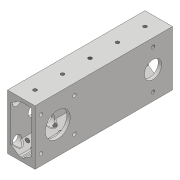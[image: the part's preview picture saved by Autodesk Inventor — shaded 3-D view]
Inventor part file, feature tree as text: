
AUTODESK INVENTOR PART (.ipt)
format: ipt  version: 2018 (Build 220112000, 112)  size: 839,680 bytes
history: native  units: mm
features: sketch x7, hole x5, extrude x3, chamfer x3, other x3, fillet x2, shell x1, pattern_linear x1, mirror x1, reference x1, projected_geometry x1
ambient origin geometry x8: Origin, YZ Plane, XZ Plane, XY Plane, X Axis, Y Axis, Z Axis, Center Point
bodies: Solid1 (feature_tree)
feature tree (28):
  extrude  "Extrusion1"  Depth=25.4mm
  shell  "Shell1"  Thickness=127.0mm
  chamfer  "Chamfer1"  Distance=23.0mm
  chamfer  "Chamfer2"  Distance=50.8mm
  chamfer  "Chamfer3"  Distance=16.0mm
  sketch  "Sketch2"  dims[d4=3.175mm]
  hole  "Hole1"  [1 undecoded]
  hole  "Hole2"  [1 undecoded]
  extrude  "Extrusion2"  Depth=3.0mm
  extrude  "Extrusion3"  Depth=3.0mm
  hole  "Hole4"  [1 undecoded]
  hole  "Hole5"  [1 undecoded]
  fillet  "Fillet3"  Radius=8.0mm
  pattern_linear  "Rectangular Pattern1"  Spacing1=1.5mm  [1 undecoded]
  mirror  "Mirror1"
  hole  "Hole6"  [1 undecoded]
  fillet  "Fillet4"  Radius=38.1mm
  sketch  "Sketch1"  dims[d0=50.8mm d1=25.4mm d2=127.0mm d3=0.0mm]
  sketch  "Sketch3"  dims[d5=31.0mm]
  sketch  "Sketch4"  dims[d6=31.0mm]
  sketch  "Sketch6"  dims[d7=21.0mm]
  sketch  "Sketch7"  dims[d8=3.2mm d9=6.0mm d10=8.0mm d11=22.225mm d12=90.0deg d13=8.0mm d14=20.594885mm]
  reference  "Reference1"
  sketch  "Sketch8"  dims[d15=10.0mm d16=6.0mm d17=6.5mm d18=3.0mm d19=90.0deg d20=8.0mm d21=20.594885mm d22=23.0mm d23=50.8mm d24=0.0mm d25=16.0mm d26=18.0mm d27=50.8mm d28=0.0mm d40=3.242mm d41=100.0mm d42=6.5mm d43=3.0mm d44=90.0deg d45=11.8mm d46=20.594885mm d47=36.0mm d48=3.242mm d49=100.0mm d50=6.5mm d51=3.0mm d52=90.0deg d53=11.8mm d54=20.594885mm d55=50.8mm d56=8.0mm d57=5.5mm d58=45.0deg d59=5.5mm d60=8.0mm d61=45.0deg d62=8.0mm d63=5.5mm d64=45.0deg d70=1.5mm d72=20.0mm d74=50.8mm d75=38.1mm d76=14.0mm d77=3.242mm d78=8.0mm d79=4.0mm d80=2.0mm d81=90.0deg d82=11.8mm d83=20.594885mm d84=3.0mm]
  projected_geometry  "Projected Loop1"
  parser-record x1  (decoder bookkeeping rows leaked as tree rows — omitted from the tree; the rows remain in map.json)
  other  "AMR_Transm2.iam"
  other  "7804K147_STAINLESS STEEL BALL BEARING:2"
note: 6 required parameter values undecoded (feature->parameter linkage not recoverable at this tier; creation-order binding heuristic only, values carry confidence <= 0.55)
note: 1 file-system path scrubbed to <path> (originals preserved in map.json)
